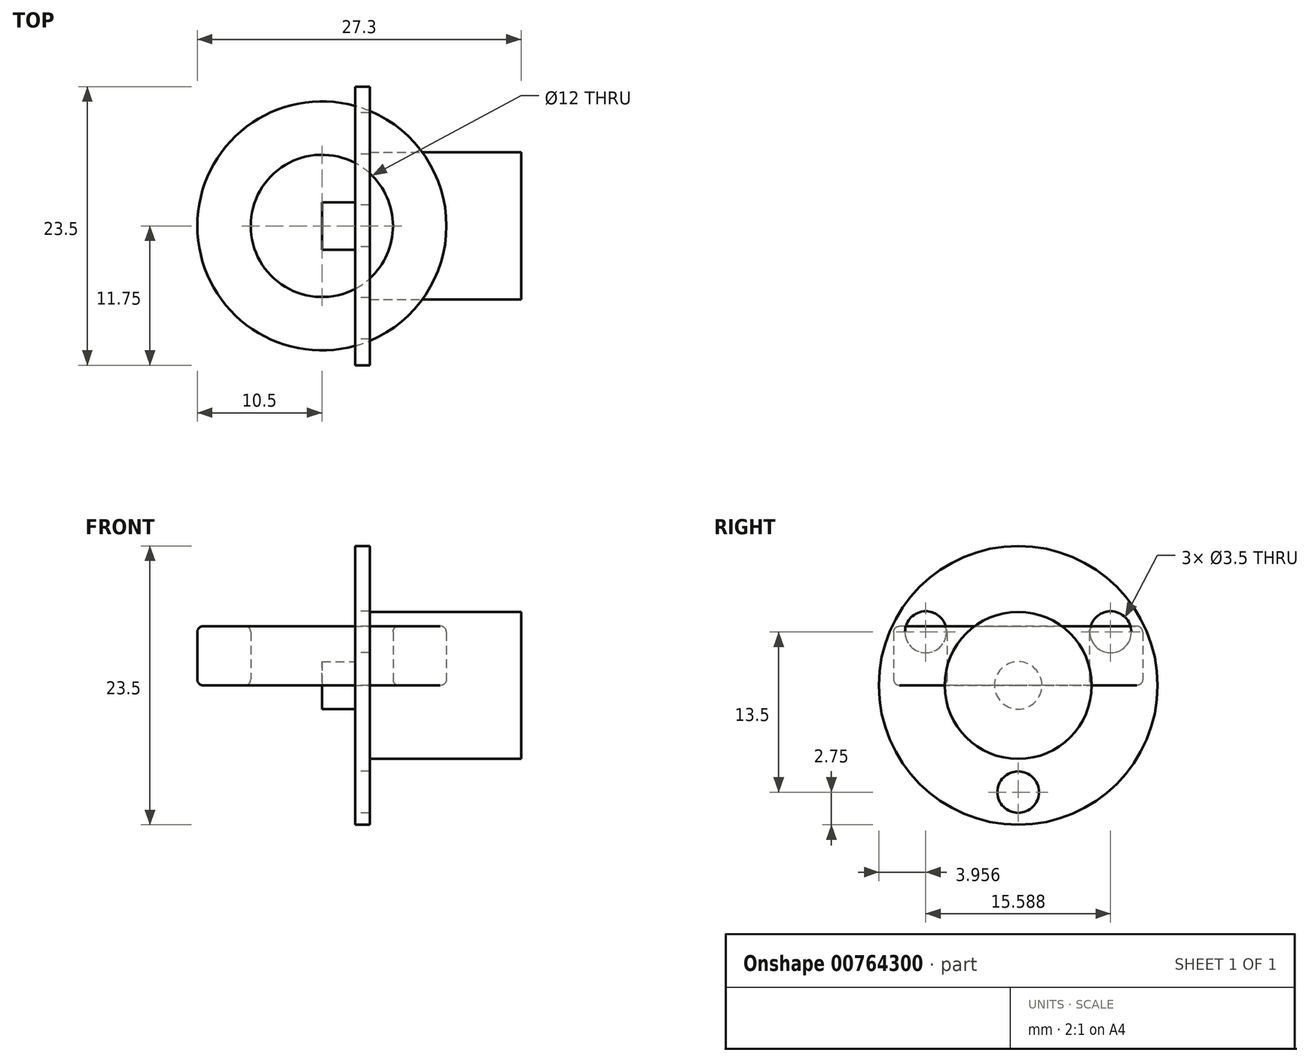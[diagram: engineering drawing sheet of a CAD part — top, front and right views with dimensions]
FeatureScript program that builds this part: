
annotation { "Feature Type Name" : "Feature", "Feature Type Description" : "" }
export const myFeature = defineFeature(function(context is Context, id is Id, definition is map)
    precondition{}
    {
        {
            var Q0;
            Q0=qCreatedBy(makeId("Front.planeOp"),FACE);
            var sketch = newSketch(context, id + "F0", { "sketchPlane" : qUnion([Q0])});
            skLineSegment(sketch, "E0", {"start": v(2.8, 2) * mm, "end": v(2.8, 11.75) * mm});
            skLineSegment(sketch, "E1", {"start": v(2.8, 11.75) * mm, "end": v(4.05, 11.75) * mm});
            skLineSegment(sketch, "E2", {"start": v(4.05, 11.75) * mm, "end": v(4.05, 6.2) * mm});
            skLineSegment(sketch, "E3", {"start": v(4.05, 6.2) * mm, "end": v(16.8, 6.2) * mm});
            skLineSegment(sketch, "E4", {"start": v(16.8, 6.2) * mm, "end": v(16.8, 0) * mm});
            skLineSegment(sketch, "E5", {"start": v(2.8, 2) * mm, "end": v(0, 2) * mm});
            skLineSegment(sketch, "E6", {"start": v(0, 2) * mm, "end": v(0, 0) * mm});
            skLineSegment(sketch, "E7", {"start": v(0, 0) * mm, "end": v(16.8, 0) * mm});
            skLineSegment(sketch, "E8", {"start": v(0, 0) * mm, "end": v(-4.5, 0) * mm, "construction": true});
            skSolve(sketch);
        }
        {
            var Q0;
            Q0 = qSketchRegion(id + "F0", true);
            var Q1;
            Q1=sQuery(id+"F0.wireOp",EDGE,"E8");
            revolve(context, id + "F1", {"surfaceOperationType" : NewSurfaceOperationType.NEW, "entities" : qUnion([Q0]), "axis" : qUnion([Q1]), "revolveType" : RevolveType.FULL});
        }
        {
            var Q0;
            Q0=makeQuery(id+"F1.opRevolve","SWEPT_FACE",FACE,{"disambiguationData":[OSD([sQuery(id+"F0.wireOp",EDGE,"E0")])]});
            var sketch = newSketch(context, id + "F2", { "sketchPlane" : qUnion([Q0])});
            skCircle(sketch, "E9", {"center": v(0, 0) * mm, "radius": 9 * mm, "construction": true});
            skCircle(sketch, "E10", {"center": v(-7.8, 4.5) * mm, "radius": 1.75 * mm});
            skCircle(sketch, "E11", {"center": v(7.8, 4.5) * mm, "radius": 1.75 * mm});
            skCircle(sketch, "E12", {"center": v(0, -9) * mm, "radius": 1.75 * mm});
            skLineSegment(sketch, "E13", {"start": v(0, -9) * mm, "end": v(7.8, 4.5) * mm, "construction": true});
            skLineSegment(sketch, "E14", {"start": v(7.8, 4.5) * mm, "end": v(-7.8, 4.5) * mm, "construction": true});
            skLineSegment(sketch, "E15", {"start": v(-7.8, 4.5) * mm, "end": v(0, -9) * mm, "construction": true});
            skSolve(sketch);
        }
        {
            var Q0;
            Q0=makeQuery(id+"F2.imprint","IMPRINT",FACE,{"disambiguationData":[TD([[makeQuery(id+"F2.imprint","IMPRINT",EDGE,{"derivedFrom":sQuery(id+"F2.wireOp",EDGE,"E10")}),1.0]])]});
            var Q1;
            Q1=makeQuery(id+"F2.imprint","IMPRINT",FACE,{"disambiguationData":[TD([[makeQuery(id+"F2.imprint","IMPRINT",EDGE,{"derivedFrom":sQuery(id+"F2.wireOp",EDGE,"E11")}),1.0]])]});
            var Q2;
            Q2=makeQuery(id+"F2.imprint","IMPRINT",FACE,{"disambiguationData":[TD([[makeQuery(id+"F2.imprint","IMPRINT",EDGE,{"derivedFrom":sQuery(id+"F2.wireOp",EDGE,"E12")}),1.0]])]});
            extrude(context, id + "F3", {"entities" : qUnion([Q0, Q1, Q2]), "operationType" : NewBodyOperationType.REMOVE, "endBound" : BoundingType.THROUGH_ALL, "oppositeDirection" : true, "depth" : 25 * mm, "offsetDistance" : 25 * mm});
        }
        {
            var Q0;
            Q0=qCreatedBy(makeId("Front.planeOp"),FACE);
            var sketch = newSketch(context, id + "F4", { "sketchPlane" : qUnion([Q0])});
            skLineSegment(sketch, "E16.bottom", {"start": v(6, 0) * mm, "end": v(10.5, 0) * mm});
            skLineSegment(sketch, "E16.top", {"start": v(6, 5) * mm, "end": v(10.5, 5) * mm});
            skLineSegment(sketch, "E16.left", {"start": v(6, 0) * mm, "end": v(6, 5) * mm});
            skLineSegment(sketch, "E16.right", {"start": v(10.5, 0) * mm, "end": v(10.5, 5) * mm});
            skLineSegment(sketch, "E17", {"start": v(0, 0) * mm, "end": v(0, 0.71) * mm, "construction": true});
            skSolve(sketch);
        }
        {
            var Q0;
            Q0=makeQuery(id+"F4.imprint","IMPRINT",FACE,{"disambiguationData":[TD([[makeQuery(id+"F4.imprint","IMPRINT",EDGE,{"derivedFrom":sQuery(id+"F4.wireOp",EDGE,"E16.bottom")}),1.0]])]});
            var Q1;
            Q1=sQuery(id+"F4.wireOp",EDGE,"E17");
            revolve(context, id + "F5", {"surfaceOperationType" : NewSurfaceOperationType.NEW, "entities" : qUnion([Q0]), "axis" : qUnion([Q1]), "revolveType" : RevolveType.FULL});
        }
        {
            var Q0;
            Q0=makeQuery(id+"F5.opRevolve","SWEPT_EDGE",EDGE,{"disambiguationData":[OSD([sQuery(id+"F4.wireOp",EDGE,"E16.top"),sQuery(id+"F4.wireOp",EDGE,"E16.right")])]});
            var Q1;
            Q1=makeQuery(id+"F5.opRevolve","SWEPT_EDGE",EDGE,{"disambiguationData":[OSD([sQuery(id+"F4.wireOp",EDGE,"E16.top"),sQuery(id+"F4.wireOp",EDGE,"E16.left")])]});
            var Q2;
            Q2=makeQuery(id+"F5.opRevolve","SWEPT_EDGE",EDGE,{"disambiguationData":[OSD([sQuery(id+"F4.wireOp",EDGE,"E16.bottom"),sQuery(id+"F4.wireOp",EDGE,"E16.left")])]});
            var Q3;
            Q3=makeQuery(id+"F5.opRevolve","SWEPT_EDGE",EDGE,{"disambiguationData":[OSD([sQuery(id+"F4.wireOp",EDGE,"E16.bottom"),sQuery(id+"F4.wireOp",EDGE,"E16.right")])]});
            fillet(context, id + "F6", {"entities" : qUnion([Q0, Q1, Q2, Q3]), "radius" : 0.5 * mm, "tangentPropagation" : true, "allowEdgeOverflow" : false});
        }
    });
